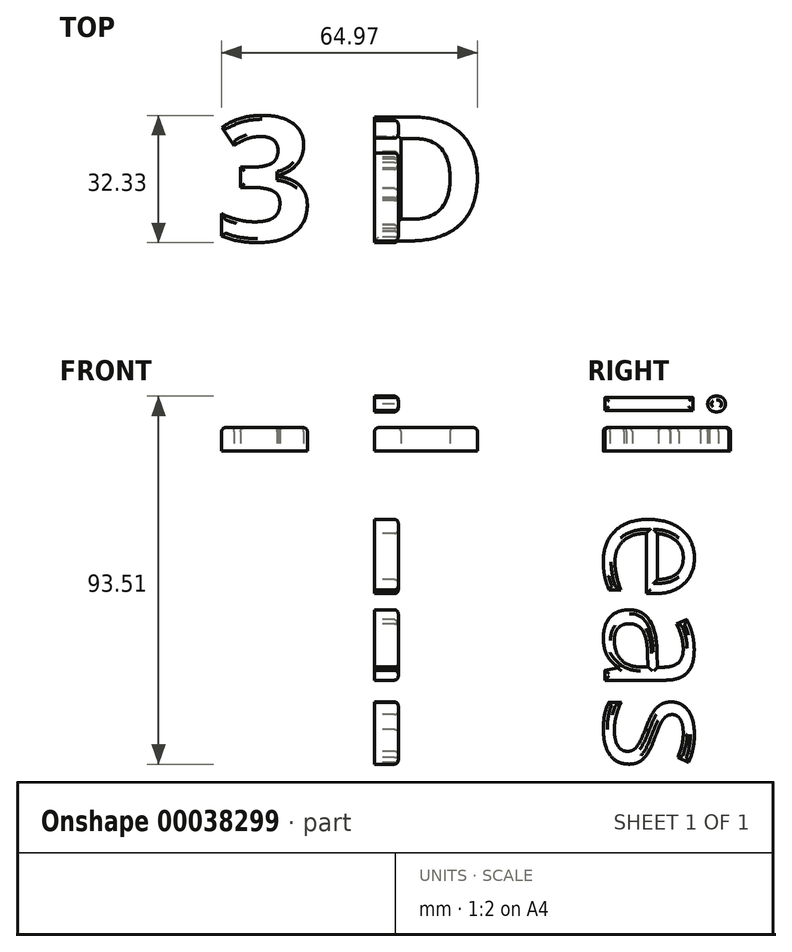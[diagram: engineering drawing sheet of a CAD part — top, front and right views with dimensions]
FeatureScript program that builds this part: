
annotation { "Feature Type Name" : "Feature", "Feature Type Description" : "" }
export const myFeature = defineFeature(function(context is Context, id is Id, definition is map)
    precondition{}
    {
        {
            var Q0;
            Q0=qCreatedBy(makeId("Top.planeOp"),FACE);
            var sketch = newSketch(context, id + "F0", { "sketchPlane" : qUnion([Q0])});
            skText(sketch, "E0", { "text": "3 D", "fontName": "OpenSans-Bold.ttf"});
            const initialGuessF0  = {"E0": [-0.06666, 0, 1, 0, 0.03172]};
            skSetInitialGuess(sketch, initialGuessF0);
            skSolve(sketch);
        }
        {
            var Q0;
            Q0=makeQuery(id+"F0.imprint","IMPRINT",FACE,{"disambiguationData":[TD([[makeQuery(id+"F0.imprint","IMPRINT",EDGE,{"derivedFrom":sQuery(id+"F0.wireOp",EDGE,"E0.sketch_text.stroke-0")}),-1.0]])]});
            var Q1;
            Q1=makeQuery(id+"F0.imprint","IMPRINT",FACE,{"disambiguationData":[TD([[makeQuery(id+"F0.imprint","IMPRINT",EDGE,{"derivedFrom":sQuery(id+"F0.wireOp",EDGE,"1949aad5-839d-4fb3-a845-ca18cb88f10a.sketch_text.stroke-0")}),-1.0]])]});
            var Q2;
            Q2=makeQuery(id+"F0.imprint","IMPRINT",FACE,{"disambiguationData":[TD([[makeQuery(id+"F0.imprint","IMPRINT",EDGE,{"derivedFrom":sQuery(id+"F0.wireOp",EDGE,"1949aad5-839d-4fb3-a845-ca18cb88f10a.sketch_text.stroke-9")}),-1.0]])]});
            var Q3;
            Q3=makeQuery(id+"F0.imprint","IMPRINT",FACE,{"disambiguationData":[TD([[makeQuery(id+"F0.imprint","IMPRINT",EDGE,{"derivedFrom":sQuery(id+"F0.wireOp",EDGE,"1949aad5-839d-4fb3-a845-ca18cb88f10a.sketch_text.stroke-41")}),-1.0]])]});
            var Q4;
            Q4=makeQuery(id+"F0.imprint","IMPRINT",FACE,{"disambiguationData":[TD([[makeQuery(id+"F0.imprint","IMPRINT",EDGE,{"derivedFrom":sQuery(id+"F0.wireOp",EDGE,"E0.sketch_text.stroke-27")}),-1.0]])]});
            var Q5;
            Q5=makeQuery(id+"F0.imprint","IMPRINT",FACE,{"disambiguationData":[TD([[makeQuery(id+"F0.imprint","IMPRINT",EDGE,{"derivedFrom":sQuery(id+"F0.wireOp",EDGE,"1949aad5-839d-4fb3-a845-ca18cb88f10a.sketch_text.stroke-16")}),-1.0]])]});
            extrude(context, id + "F1", {"entities" : qUnion([Q0, Q1, Q2, Q3, Q4, Q5]), "depth" : 6 * mm});
        }
        {
            var Q0;
            Q0=makeQuery(id+"F1.opExtrude","CAP_EDGE",EDGE,{"disambiguationData":[OSD([sQuery(id+"F0.wireOp",EDGE,"E0.sketch_text.stroke-30")])],"isStart":true});
            cPlane(context, id + "F2", {"entities" : qUnion([Q0]), "cplaneType" : CPlaneType.LINE_ANGLE, "offset" : 150 * mm, "angle" : 90 * degree, "width" : 150 * mm, "height" : 150 * mm});
        }
        {
            var Q0;
            Q0=qCreatedBy(id+"F2.planeOp",FACE);
            var sketch = newSketch(context, id + "F3", { "sketchPlane" : qUnion([Q0])});
            skText(sketch, "E1", { "text": "i", "fontName": "OpenSans-Regular.ttf"});
            skText(sketch, "E2", { "text": "eas", "fontName": "OpenSans-Regular.ttf"});
            const initialGuessF3  = {"E1": [0, 0.01729, 0, -1, 0.03], "E2": [0, -0.015, 0, -1, 0.03]};
            skSetInitialGuess(sketch, initialGuessF3);
            skSolve(sketch);
        }
        {
            var Q0;
            Q0=qSketchRegion(id+"F3",true);
            extrude(context, id + "F4", {"entities" : qUnion([Q0]), "depth" : 6 * mm});
        }
        {
            var Q0;
            Q0=makeQuery(id+"F1.opExtrude","CAP_EDGE",EDGE,{"disambiguationData":[OSD([sQuery(id+"F0.wireOp",EDGE,"E0.sketch_text.stroke-6")])],"isStart":false});
            var Q1;
            Q1=makeQuery(id+"F1.opExtrude","CAP_EDGE",EDGE,{"disambiguationData":[OSD([sQuery(id+"F0.wireOp",EDGE,"E0.sketch_text.stroke-0")])],"isStart":false});
            var Q2;
            Q2=makeQuery(id+"F1.opExtrude","CAP_EDGE",EDGE,{"disambiguationData":[OSD([sQuery(id+"F0.wireOp",EDGE,"E0.sketch_text.stroke-23")])],"isStart":false});
            var Q3;
            Q3=makeQuery(id+"F1.opExtrude","CAP_EDGE",EDGE,{"disambiguationData":[OSD([sQuery(id+"F0.wireOp",EDGE,"E0.sketch_text.stroke-21")])],"isStart":false});
            var Q4;
            Q4=makeQuery(id+"F1.opExtrude","CAP_EDGE",EDGE,{"disambiguationData":[OSD([sQuery(id+"F0.wireOp",EDGE,"E0.sketch_text.stroke-16")])],"isStart":false});
            var Q5;
            Q5=makeQuery(id+"F1.opExtrude","CAP_EDGE",EDGE,{"disambiguationData":[OSD([sQuery(id+"F0.wireOp",EDGE,"E0.sketch_text.stroke-14")])],"isStart":false});
            var Q6;
            Q6=makeQuery(id+"F1.opExtrude","CAP_EDGE",EDGE,{"disambiguationData":[OSD([sQuery(id+"F0.wireOp",EDGE,"E0.sketch_text.stroke-8")])],"isStart":false});
            var Q7;
            Q7=makeQuery(id+"F1.opExtrude","CAP_EDGE",EDGE,{"disambiguationData":[OSD([sQuery(id+"F0.wireOp",EDGE,"E0.sketch_text.stroke-30")])],"isStart":false});
            var Q8;
            Q8=makeQuery(id+"F1.opExtrude","CAP_EDGE",EDGE,{"disambiguationData":[OSD([sQuery(id+"F0.wireOp",EDGE,"E0.sketch_text.stroke-31")])],"isStart":false});
            var Q9;
            Q9=makeQuery(id+"F1.opExtrude","CAP_EDGE",EDGE,{"disambiguationData":[OSD([sQuery(id+"F0.wireOp",EDGE,"E0.sketch_text.stroke-36")])],"isStart":false});
            var Q10;
            Q10=makeQuery(id+"F1.opExtrude","CAP_EDGE",EDGE,{"disambiguationData":[OSD([sQuery(id+"F0.wireOp",EDGE,"E0.sketch_text.stroke-35")])],"isStart":false});
            var Q11;
            Q11=makeQuery(id+"F4.opExtrude","CAP_FACE",FACE,{"disambiguationData":[OSD([sQuery(id+"F3.wireOp",EDGE,"9d5f91f5-e47f-4394-aaea-d1b4c45abdbb.sketch_text.stroke-0"),sQuery(id+"F3.wireOp",EDGE,"9d5f91f5-e47f-4394-aaea-d1b4c45abdbb.sketch_text.stroke-1"),sQuery(id+"F3.wireOp",EDGE,"9d5f91f5-e47f-4394-aaea-d1b4c45abdbb.sketch_text.stroke-2"),sQuery(id+"F3.wireOp",EDGE,"9d5f91f5-e47f-4394-aaea-d1b4c45abdbb.sketch_text.stroke-3")])],"isStart":false});
            var Q12;
            Q12=makeQuery(id+"F4.opExtrude","CAP_FACE",FACE,{"disambiguationData":[OSD([sQuery(id+"F3.wireOp",EDGE,"9d5f91f5-e47f-4394-aaea-d1b4c45abdbb.sketch_text.stroke-4"),sQuery(id+"F3.wireOp",EDGE,"9d5f91f5-e47f-4394-aaea-d1b4c45abdbb.sketch_text.stroke-5"),sQuery(id+"F3.wireOp",EDGE,"9d5f91f5-e47f-4394-aaea-d1b4c45abdbb.sketch_text.stroke-6"),sQuery(id+"F3.wireOp",EDGE,"9d5f91f5-e47f-4394-aaea-d1b4c45abdbb.sketch_text.stroke-7"),sQuery(id+"F3.wireOp",EDGE,"9d5f91f5-e47f-4394-aaea-d1b4c45abdbb.sketch_text.stroke-8"),sQuery(id+"F3.wireOp",EDGE,"9d5f91f5-e47f-4394-aaea-d1b4c45abdbb.sketch_text.stroke-9"),sQuery(id+"F3.wireOp",EDGE,"9d5f91f5-e47f-4394-aaea-d1b4c45abdbb.sketch_text.stroke-10"),sQuery(id+"F3.wireOp",EDGE,"9d5f91f5-e47f-4394-aaea-d1b4c45abdbb.sketch_text.stroke-11")])],"isStart":false});
            var Q13;
            Q13=makeQuery(id+"F4.opExtrude","CAP_FACE",FACE,{"disambiguationData":[OSD([sQuery(id+"F3.wireOp",EDGE,"742c4371-0e1b-4878-b02d-ca1a3e051308.sketch_text.stroke-0"),sQuery(id+"F3.wireOp",EDGE,"742c4371-0e1b-4878-b02d-ca1a3e051308.sketch_text.stroke-1"),sQuery(id+"F3.wireOp",EDGE,"742c4371-0e1b-4878-b02d-ca1a3e051308.sketch_text.stroke-2"),sQuery(id+"F3.wireOp",EDGE,"742c4371-0e1b-4878-b02d-ca1a3e051308.sketch_text.stroke-3"),sQuery(id+"F3.wireOp",EDGE,"742c4371-0e1b-4878-b02d-ca1a3e051308.sketch_text.stroke-4"),sQuery(id+"F3.wireOp",EDGE,"742c4371-0e1b-4878-b02d-ca1a3e051308.sketch_text.stroke-5"),sQuery(id+"F3.wireOp",EDGE,"742c4371-0e1b-4878-b02d-ca1a3e051308.sketch_text.stroke-6"),sQuery(id+"F3.wireOp",EDGE,"742c4371-0e1b-4878-b02d-ca1a3e051308.sketch_text.stroke-7"),sQuery(id+"F3.wireOp",EDGE,"742c4371-0e1b-4878-b02d-ca1a3e051308.sketch_text.stroke-8"),sQuery(id+"F3.wireOp",EDGE,"742c4371-0e1b-4878-b02d-ca1a3e051308.sketch_text.stroke-9"),sQuery(id+"F3.wireOp",EDGE,"742c4371-0e1b-4878-b02d-ca1a3e051308.sketch_text.stroke-10"),sQuery(id+"F3.wireOp",EDGE,"742c4371-0e1b-4878-b02d-ca1a3e051308.sketch_text.stroke-11"),sQuery(id+"F3.wireOp",EDGE,"742c4371-0e1b-4878-b02d-ca1a3e051308.sketch_text.stroke-12"),sQuery(id+"F3.wireOp",EDGE,"742c4371-0e1b-4878-b02d-ca1a3e051308.sketch_text.stroke-13"),sQuery(id+"F3.wireOp",EDGE,"742c4371-0e1b-4878-b02d-ca1a3e051308.sketch_text.stroke-14"),sQuery(id+"F3.wireOp",EDGE,"742c4371-0e1b-4878-b02d-ca1a3e051308.sketch_text.stroke-15"),sQuery(id+"F3.wireOp",EDGE,"742c4371-0e1b-4878-b02d-ca1a3e051308.sketch_text.stroke-16"),sQuery(id+"F3.wireOp",EDGE,"742c4371-0e1b-4878-b02d-ca1a3e051308.sketch_text.stroke-17"),sQuery(id+"F3.wireOp",EDGE,"742c4371-0e1b-4878-b02d-ca1a3e051308.sketch_text.stroke-18")])],"isStart":false});
            var Q14;
            Q14=makeQuery(id+"F4.opExtrude","CAP_FACE",FACE,{"disambiguationData":[OSD([sQuery(id+"F3.wireOp",EDGE,"742c4371-0e1b-4878-b02d-ca1a3e051308.sketch_text.stroke-19"),sQuery(id+"F3.wireOp",EDGE,"742c4371-0e1b-4878-b02d-ca1a3e051308.sketch_text.stroke-20"),sQuery(id+"F3.wireOp",EDGE,"742c4371-0e1b-4878-b02d-ca1a3e051308.sketch_text.stroke-21"),sQuery(id+"F3.wireOp",EDGE,"742c4371-0e1b-4878-b02d-ca1a3e051308.sketch_text.stroke-22"),sQuery(id+"F3.wireOp",EDGE,"742c4371-0e1b-4878-b02d-ca1a3e051308.sketch_text.stroke-23"),sQuery(id+"F3.wireOp",EDGE,"742c4371-0e1b-4878-b02d-ca1a3e051308.sketch_text.stroke-24"),sQuery(id+"F3.wireOp",EDGE,"742c4371-0e1b-4878-b02d-ca1a3e051308.sketch_text.stroke-25"),sQuery(id+"F3.wireOp",EDGE,"742c4371-0e1b-4878-b02d-ca1a3e051308.sketch_text.stroke-26"),sQuery(id+"F3.wireOp",EDGE,"742c4371-0e1b-4878-b02d-ca1a3e051308.sketch_text.stroke-27"),sQuery(id+"F3.wireOp",EDGE,"742c4371-0e1b-4878-b02d-ca1a3e051308.sketch_text.stroke-28"),sQuery(id+"F3.wireOp",EDGE,"742c4371-0e1b-4878-b02d-ca1a3e051308.sketch_text.stroke-29"),sQuery(id+"F3.wireOp",EDGE,"742c4371-0e1b-4878-b02d-ca1a3e051308.sketch_text.stroke-30"),sQuery(id+"F3.wireOp",EDGE,"742c4371-0e1b-4878-b02d-ca1a3e051308.sketch_text.stroke-31"),sQuery(id+"F3.wireOp",EDGE,"742c4371-0e1b-4878-b02d-ca1a3e051308.sketch_text.stroke-32"),sQuery(id+"F3.wireOp",EDGE,"742c4371-0e1b-4878-b02d-ca1a3e051308.sketch_text.stroke-33"),sQuery(id+"F3.wireOp",EDGE,"742c4371-0e1b-4878-b02d-ca1a3e051308.sketch_text.stroke-34"),sQuery(id+"F3.wireOp",EDGE,"742c4371-0e1b-4878-b02d-ca1a3e051308.sketch_text.stroke-35"),sQuery(id+"F3.wireOp",EDGE,"742c4371-0e1b-4878-b02d-ca1a3e051308.sketch_text.stroke-36"),sQuery(id+"F3.wireOp",EDGE,"742c4371-0e1b-4878-b02d-ca1a3e051308.sketch_text.stroke-37"),sQuery(id+"F3.wireOp",EDGE,"742c4371-0e1b-4878-b02d-ca1a3e051308.sketch_text.stroke-38"),sQuery(id+"F3.wireOp",EDGE,"742c4371-0e1b-4878-b02d-ca1a3e051308.sketch_text.stroke-39"),sQuery(id+"F3.wireOp",EDGE,"742c4371-0e1b-4878-b02d-ca1a3e051308.sketch_text.stroke-40"),sQuery(id+"F3.wireOp",EDGE,"742c4371-0e1b-4878-b02d-ca1a3e051308.sketch_text.stroke-41"),sQuery(id+"F3.wireOp",EDGE,"742c4371-0e1b-4878-b02d-ca1a3e051308.sketch_text.stroke-42"),sQuery(id+"F3.wireOp",EDGE,"742c4371-0e1b-4878-b02d-ca1a3e051308.sketch_text.stroke-43"),sQuery(id+"F3.wireOp",EDGE,"742c4371-0e1b-4878-b02d-ca1a3e051308.sketch_text.stroke-44"),sQuery(id+"F3.wireOp",EDGE,"742c4371-0e1b-4878-b02d-ca1a3e051308.sketch_text.stroke-45")])],"isStart":false});
            var Q15;
            Q15=makeQuery(id+"F4.opExtrude","CAP_FACE",FACE,{"disambiguationData":[OSD([sQuery(id+"F3.wireOp",EDGE,"742c4371-0e1b-4878-b02d-ca1a3e051308.sketch_text.stroke-46"),sQuery(id+"F3.wireOp",EDGE,"742c4371-0e1b-4878-b02d-ca1a3e051308.sketch_text.stroke-47"),sQuery(id+"F3.wireOp",EDGE,"742c4371-0e1b-4878-b02d-ca1a3e051308.sketch_text.stroke-48"),sQuery(id+"F3.wireOp",EDGE,"742c4371-0e1b-4878-b02d-ca1a3e051308.sketch_text.stroke-49"),sQuery(id+"F3.wireOp",EDGE,"742c4371-0e1b-4878-b02d-ca1a3e051308.sketch_text.stroke-50"),sQuery(id+"F3.wireOp",EDGE,"742c4371-0e1b-4878-b02d-ca1a3e051308.sketch_text.stroke-51"),sQuery(id+"F3.wireOp",EDGE,"742c4371-0e1b-4878-b02d-ca1a3e051308.sketch_text.stroke-52"),sQuery(id+"F3.wireOp",EDGE,"742c4371-0e1b-4878-b02d-ca1a3e051308.sketch_text.stroke-53"),sQuery(id+"F3.wireOp",EDGE,"742c4371-0e1b-4878-b02d-ca1a3e051308.sketch_text.stroke-54"),sQuery(id+"F3.wireOp",EDGE,"742c4371-0e1b-4878-b02d-ca1a3e051308.sketch_text.stroke-55"),sQuery(id+"F3.wireOp",EDGE,"742c4371-0e1b-4878-b02d-ca1a3e051308.sketch_text.stroke-56"),sQuery(id+"F3.wireOp",EDGE,"742c4371-0e1b-4878-b02d-ca1a3e051308.sketch_text.stroke-57"),sQuery(id+"F3.wireOp",EDGE,"742c4371-0e1b-4878-b02d-ca1a3e051308.sketch_text.stroke-58"),sQuery(id+"F3.wireOp",EDGE,"742c4371-0e1b-4878-b02d-ca1a3e051308.sketch_text.stroke-59"),sQuery(id+"F3.wireOp",EDGE,"742c4371-0e1b-4878-b02d-ca1a3e051308.sketch_text.stroke-60"),sQuery(id+"F3.wireOp",EDGE,"742c4371-0e1b-4878-b02d-ca1a3e051308.sketch_text.stroke-61"),sQuery(id+"F3.wireOp",EDGE,"742c4371-0e1b-4878-b02d-ca1a3e051308.sketch_text.stroke-62"),sQuery(id+"F3.wireOp",EDGE,"742c4371-0e1b-4878-b02d-ca1a3e051308.sketch_text.stroke-63"),sQuery(id+"F3.wireOp",EDGE,"742c4371-0e1b-4878-b02d-ca1a3e051308.sketch_text.stroke-64"),sQuery(id+"F3.wireOp",EDGE,"742c4371-0e1b-4878-b02d-ca1a3e051308.sketch_text.stroke-65"),sQuery(id+"F3.wireOp",EDGE,"742c4371-0e1b-4878-b02d-ca1a3e051308.sketch_text.stroke-66"),sQuery(id+"F3.wireOp",EDGE,"742c4371-0e1b-4878-b02d-ca1a3e051308.sketch_text.stroke-67"),sQuery(id+"F3.wireOp",EDGE,"742c4371-0e1b-4878-b02d-ca1a3e051308.sketch_text.stroke-68"),sQuery(id+"F3.wireOp",EDGE,"742c4371-0e1b-4878-b02d-ca1a3e051308.sketch_text.stroke-69"),sQuery(id+"F3.wireOp",EDGE,"742c4371-0e1b-4878-b02d-ca1a3e051308.sketch_text.stroke-70")])],"isStart":false});
            var Q16;
            Q16=makeQuery(id+"F4.opExtrude","CAP_FACE",FACE,{"disambiguationData":[OSD([sQuery(id+"F3.wireOp",EDGE,"E1.sketch_text.stroke-0"),sQuery(id+"F3.wireOp",EDGE,"E1.sketch_text.stroke-1"),sQuery(id+"F3.wireOp",EDGE,"E1.sketch_text.stroke-2"),sQuery(id+"F3.wireOp",EDGE,"E1.sketch_text.stroke-3")])],"isStart":false});
            var Q17;
            Q17=makeQuery(id+"F4.opExtrude","CAP_FACE",FACE,{"disambiguationData":[OSD([sQuery(id+"F3.wireOp",EDGE,"E1.sketch_text.stroke-4"),sQuery(id+"F3.wireOp",EDGE,"E1.sketch_text.stroke-5"),sQuery(id+"F3.wireOp",EDGE,"E1.sketch_text.stroke-6"),sQuery(id+"F3.wireOp",EDGE,"E1.sketch_text.stroke-7"),sQuery(id+"F3.wireOp",EDGE,"E1.sketch_text.stroke-8"),sQuery(id+"F3.wireOp",EDGE,"E1.sketch_text.stroke-9"),sQuery(id+"F3.wireOp",EDGE,"E1.sketch_text.stroke-10"),sQuery(id+"F3.wireOp",EDGE,"E1.sketch_text.stroke-11")])],"isStart":false});
            var Q18;
            Q18=makeQuery(id+"F4.opExtrude","CAP_FACE",FACE,{"disambiguationData":[OSD([sQuery(id+"F3.wireOp",EDGE,"E2.sketch_text.stroke-0"),sQuery(id+"F3.wireOp",EDGE,"E2.sketch_text.stroke-1"),sQuery(id+"F3.wireOp",EDGE,"E2.sketch_text.stroke-2"),sQuery(id+"F3.wireOp",EDGE,"E2.sketch_text.stroke-3"),sQuery(id+"F3.wireOp",EDGE,"E2.sketch_text.stroke-4"),sQuery(id+"F3.wireOp",EDGE,"E2.sketch_text.stroke-5"),sQuery(id+"F3.wireOp",EDGE,"E2.sketch_text.stroke-6"),sQuery(id+"F3.wireOp",EDGE,"E2.sketch_text.stroke-7"),sQuery(id+"F3.wireOp",EDGE,"E2.sketch_text.stroke-8"),sQuery(id+"F3.wireOp",EDGE,"E2.sketch_text.stroke-9"),sQuery(id+"F3.wireOp",EDGE,"E2.sketch_text.stroke-10"),sQuery(id+"F3.wireOp",EDGE,"E2.sketch_text.stroke-11"),sQuery(id+"F3.wireOp",EDGE,"E2.sketch_text.stroke-12"),sQuery(id+"F3.wireOp",EDGE,"E2.sketch_text.stroke-13"),sQuery(id+"F3.wireOp",EDGE,"E2.sketch_text.stroke-14"),sQuery(id+"F3.wireOp",EDGE,"E2.sketch_text.stroke-15"),sQuery(id+"F3.wireOp",EDGE,"E2.sketch_text.stroke-16"),sQuery(id+"F3.wireOp",EDGE,"E2.sketch_text.stroke-17"),sQuery(id+"F3.wireOp",EDGE,"E2.sketch_text.stroke-18")])],"isStart":false});
            var Q19;
            Q19=makeQuery(id+"F4.opExtrude","CAP_FACE",FACE,{"disambiguationData":[OSD([sQuery(id+"F3.wireOp",EDGE,"E2.sketch_text.stroke-19"),sQuery(id+"F3.wireOp",EDGE,"E2.sketch_text.stroke-20"),sQuery(id+"F3.wireOp",EDGE,"E2.sketch_text.stroke-21"),sQuery(id+"F3.wireOp",EDGE,"E2.sketch_text.stroke-22"),sQuery(id+"F3.wireOp",EDGE,"E2.sketch_text.stroke-23"),sQuery(id+"F3.wireOp",EDGE,"E2.sketch_text.stroke-24"),sQuery(id+"F3.wireOp",EDGE,"E2.sketch_text.stroke-25"),sQuery(id+"F3.wireOp",EDGE,"E2.sketch_text.stroke-26"),sQuery(id+"F3.wireOp",EDGE,"E2.sketch_text.stroke-27"),sQuery(id+"F3.wireOp",EDGE,"E2.sketch_text.stroke-28"),sQuery(id+"F3.wireOp",EDGE,"E2.sketch_text.stroke-29"),sQuery(id+"F3.wireOp",EDGE,"E2.sketch_text.stroke-30"),sQuery(id+"F3.wireOp",EDGE,"E2.sketch_text.stroke-31"),sQuery(id+"F3.wireOp",EDGE,"E2.sketch_text.stroke-32"),sQuery(id+"F3.wireOp",EDGE,"E2.sketch_text.stroke-33"),sQuery(id+"F3.wireOp",EDGE,"E2.sketch_text.stroke-34"),sQuery(id+"F3.wireOp",EDGE,"E2.sketch_text.stroke-35"),sQuery(id+"F3.wireOp",EDGE,"E2.sketch_text.stroke-36"),sQuery(id+"F3.wireOp",EDGE,"E2.sketch_text.stroke-37"),sQuery(id+"F3.wireOp",EDGE,"E2.sketch_text.stroke-38"),sQuery(id+"F3.wireOp",EDGE,"E2.sketch_text.stroke-39"),sQuery(id+"F3.wireOp",EDGE,"E2.sketch_text.stroke-40"),sQuery(id+"F3.wireOp",EDGE,"E2.sketch_text.stroke-41"),sQuery(id+"F3.wireOp",EDGE,"E2.sketch_text.stroke-42"),sQuery(id+"F3.wireOp",EDGE,"E2.sketch_text.stroke-43"),sQuery(id+"F3.wireOp",EDGE,"E2.sketch_text.stroke-44"),sQuery(id+"F3.wireOp",EDGE,"E2.sketch_text.stroke-45")])],"isStart":false});
            var Q20;
            Q20=makeQuery(id+"F4.opExtrude","CAP_FACE",FACE,{"disambiguationData":[OSD([sQuery(id+"F3.wireOp",EDGE,"E2.sketch_text.stroke-46"),sQuery(id+"F3.wireOp",EDGE,"E2.sketch_text.stroke-47"),sQuery(id+"F3.wireOp",EDGE,"E2.sketch_text.stroke-48"),sQuery(id+"F3.wireOp",EDGE,"E2.sketch_text.stroke-49"),sQuery(id+"F3.wireOp",EDGE,"E2.sketch_text.stroke-50"),sQuery(id+"F3.wireOp",EDGE,"E2.sketch_text.stroke-51"),sQuery(id+"F3.wireOp",EDGE,"E2.sketch_text.stroke-52"),sQuery(id+"F3.wireOp",EDGE,"E2.sketch_text.stroke-53"),sQuery(id+"F3.wireOp",EDGE,"E2.sketch_text.stroke-54"),sQuery(id+"F3.wireOp",EDGE,"E2.sketch_text.stroke-55"),sQuery(id+"F3.wireOp",EDGE,"E2.sketch_text.stroke-56"),sQuery(id+"F3.wireOp",EDGE,"E2.sketch_text.stroke-57"),sQuery(id+"F3.wireOp",EDGE,"E2.sketch_text.stroke-58"),sQuery(id+"F3.wireOp",EDGE,"E2.sketch_text.stroke-59"),sQuery(id+"F3.wireOp",EDGE,"E2.sketch_text.stroke-60"),sQuery(id+"F3.wireOp",EDGE,"E2.sketch_text.stroke-61"),sQuery(id+"F3.wireOp",EDGE,"E2.sketch_text.stroke-62"),sQuery(id+"F3.wireOp",EDGE,"E2.sketch_text.stroke-63"),sQuery(id+"F3.wireOp",EDGE,"E2.sketch_text.stroke-64"),sQuery(id+"F3.wireOp",EDGE,"E2.sketch_text.stroke-65"),sQuery(id+"F3.wireOp",EDGE,"E2.sketch_text.stroke-66"),sQuery(id+"F3.wireOp",EDGE,"E2.sketch_text.stroke-67"),sQuery(id+"F3.wireOp",EDGE,"E2.sketch_text.stroke-68"),sQuery(id+"F3.wireOp",EDGE,"E2.sketch_text.stroke-69"),sQuery(id+"F3.wireOp",EDGE,"E2.sketch_text.stroke-70")])],"isStart":false});
            fillet(context, id + "F5", {"entities" : qUnion([Q0, Q1, Q2, Q3, Q4, Q5, Q6, Q7, Q8, Q9, Q10, Q11, Q12, Q13, Q14, Q15, Q16, Q17, Q18, Q19, Q20]), "radius" : 1 * mm, "tangentPropagation" : true, "allowEdgeOverflow" : false});
        }
    });
